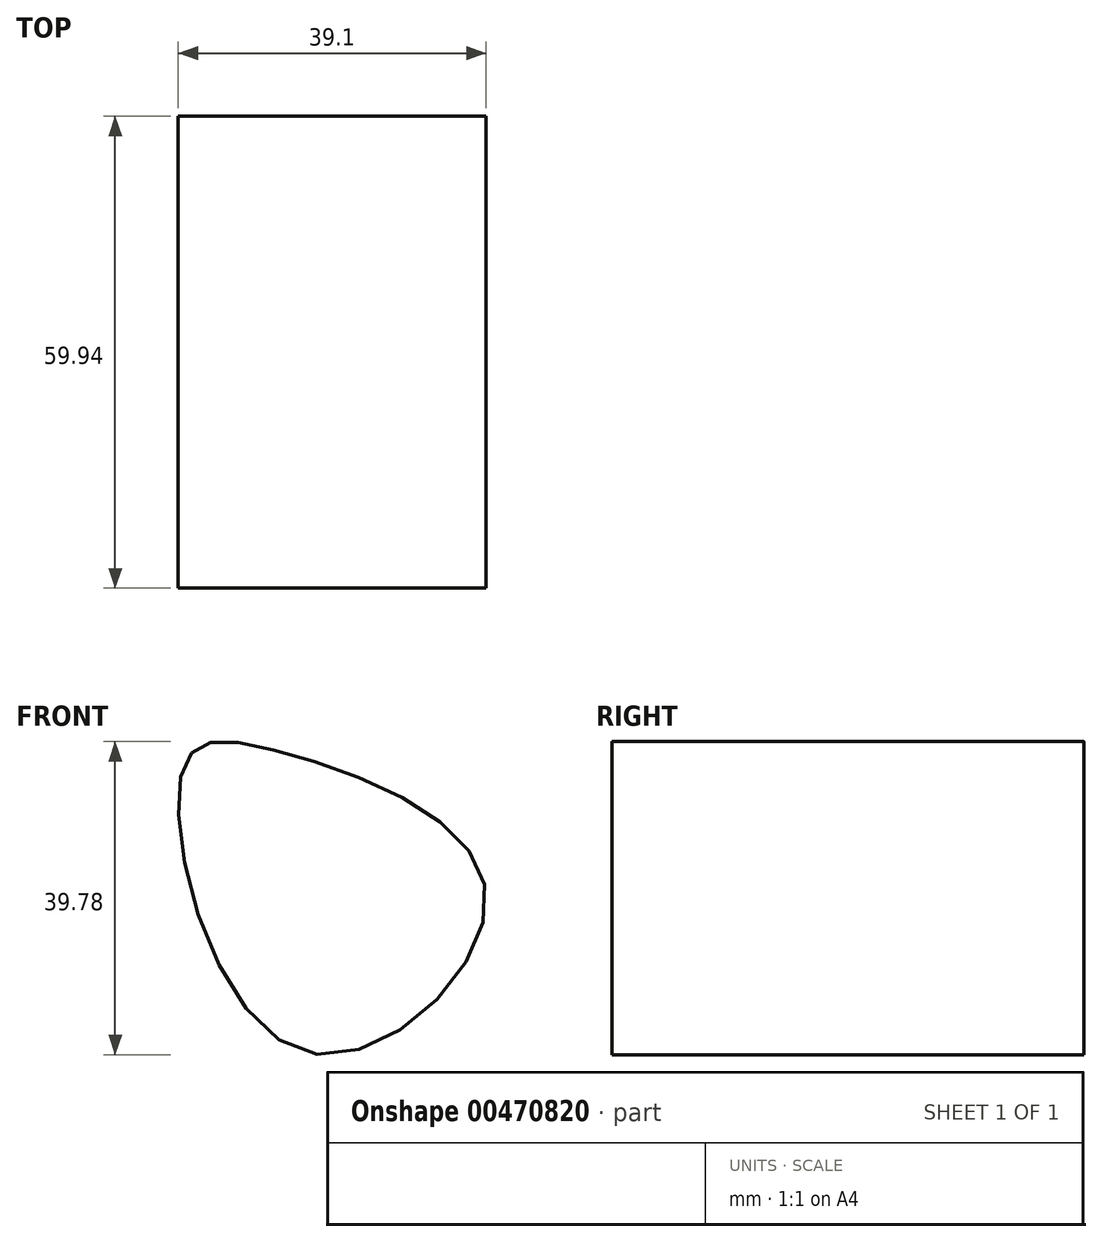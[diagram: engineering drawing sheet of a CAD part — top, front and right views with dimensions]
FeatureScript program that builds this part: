
annotation { "Feature Type Name" : "Feature", "Feature Type Description" : "" }
export const myFeature = defineFeature(function(context is Context, id is Id, definition is map)
    precondition{}
    {
        {
            var Q0;
            Q0=qCreatedBy(makeId("Front.planeOp"),FACE);
            var sketch = newSketch(context, id + "F0", { "sketchPlane" : qUnion([Q0])});
            skFitSpline(sketch, "E0", {"points": [v(21.59, 42.02) * mm, v(48.64, 23.6) * mm, v(25.33, 3.74) * mm, v(10.07, 39.43) * mm, v(21.59, 42.02) * mm]});
            skSolve(sketch);
        }
        {
            var Q0;
            Q0 = qSketchRegion(id + "F0", true);
            extrude(context, id + "F1", {"entities" : qUnion([Q0]), "depth" : 59.94 * mm});
        }
    });
